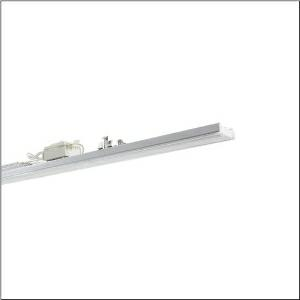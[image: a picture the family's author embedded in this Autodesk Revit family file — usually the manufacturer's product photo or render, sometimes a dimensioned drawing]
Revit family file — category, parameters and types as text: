
# Revit family: licross_21_recessed_ho_52tl1ecn4cxs
name_source: partatom
category: Lighting Fixtures
units: mm (PartAtom-declared; Revit-internal decimal feet)

## family parameters
Cut with Voids When Loaded = No
Host = Face
Light Source = No
Part Type = Normal
Room Calculation Point = No
Round Connector Dimension = Use Diameter
Shared = No

## types (1)
- --- (1 x LED, 12350 lm, 68.4 W, 4000K)
    Apparent Load = 68 VA
    CIE Flux Codes = 85 95 99 100 100
    Color Rendering = 80
    Color Temperature = 4000K
    Default Elevation = 1800 mm
    Description = Licross 21 Recessed HO, luminaire insert, of sheet steel, galvanised, coil coated, white, length: 1.500mm, width: 66mm, height: 67mm, LED rated luminous flux: 12.350lm, light colour: 840, SDCM (Standard Deviation of Colour Matching)MacAdam ≤ 3 SDCM (initial), control gear: ON/OFF Multilumen, CLOi, with plug, 3-pole, with phase selection, mains connection: 220..240V, AC, 50/60Hz, start of lifetime: 69W, end of service life: 83W, internal wiring halogen-free, primary light control with lens, of plastic, primary optical cover: cover, of PMMA, light emission: direct distribution, primary light characteristic: symmetric, protection rating (complete): IP40, insulation class (complete): insulation class I (protective earthing), certification: CE, ENEC, VDE, UKCA, protection symbol: D if used in an environment without relevant dust loads with corresponding accessories, impact resistance: IK06, permissible ambient temperature for indoor applications: -35..+30°C, corresponds to IFS (International Featured Standards) requirements for safety and quality in the food industry, reducing of maximum allowable ambient temperature of 5°C with ceiling mounting, LABS conformity tested according to VDMA 24364:2018-05, The light source and the operating device comply with the requirements of the Ecodesign Regulation (EU) 2019/2020 and are replaceable in accordance with this regulation, packaging unit: 1 piece
    Height = 58 mm
    Lamp = 1 x LED
    Lamp Light Flux = 12350 lm
    Lamp Power = 68.4 W
    Lamp count = 1
    Length = 1500 mm
    Luminous efficacy = 181 lm/W
    Manufacturer = Siteco
    ModVariant = No
    Model = 52TL1ECN4CXS
    Mounting Place = Ceiling
    Mounting Type = Pendant
    Number of Poles = 1
    OnlyDefault = Yes
    Power Factor = 1
    Product Name = Licross 21 Recessed HO
    Product group = luminaire insert | ceiling pendant
    ProductGroupID = 901
    Protection Class = Protection class I
    Protection Degree = IP 40
    RLX_Detail_Level = 1
    RLX_Emergency_Light_Flux = 0 lm
    RLX_Emergency_Type = 0
    RLX_Emergency_Type_DB = No
    RlxData = <blob elided: 22697 chars, md5=706a35c8>
    Socket = socket
    Standby Power = 0 W
    System Light Flux = 12350 lm
    System Power = 68 W
    Type Comments = factory setting: luminous flux: 100 % | (A | C | E) | 161 mA
    Type Image = l_1296930.jpg
    URL = http://relux.com
    VarID = @adj_109841
    Voltage = 0 V
    Weight = 0.00 kg
    Width = 66 mm

## geometry (parser evidence)
native form markers: Blend x4, Sweep x11
no freeform markers — native parametric forms only
